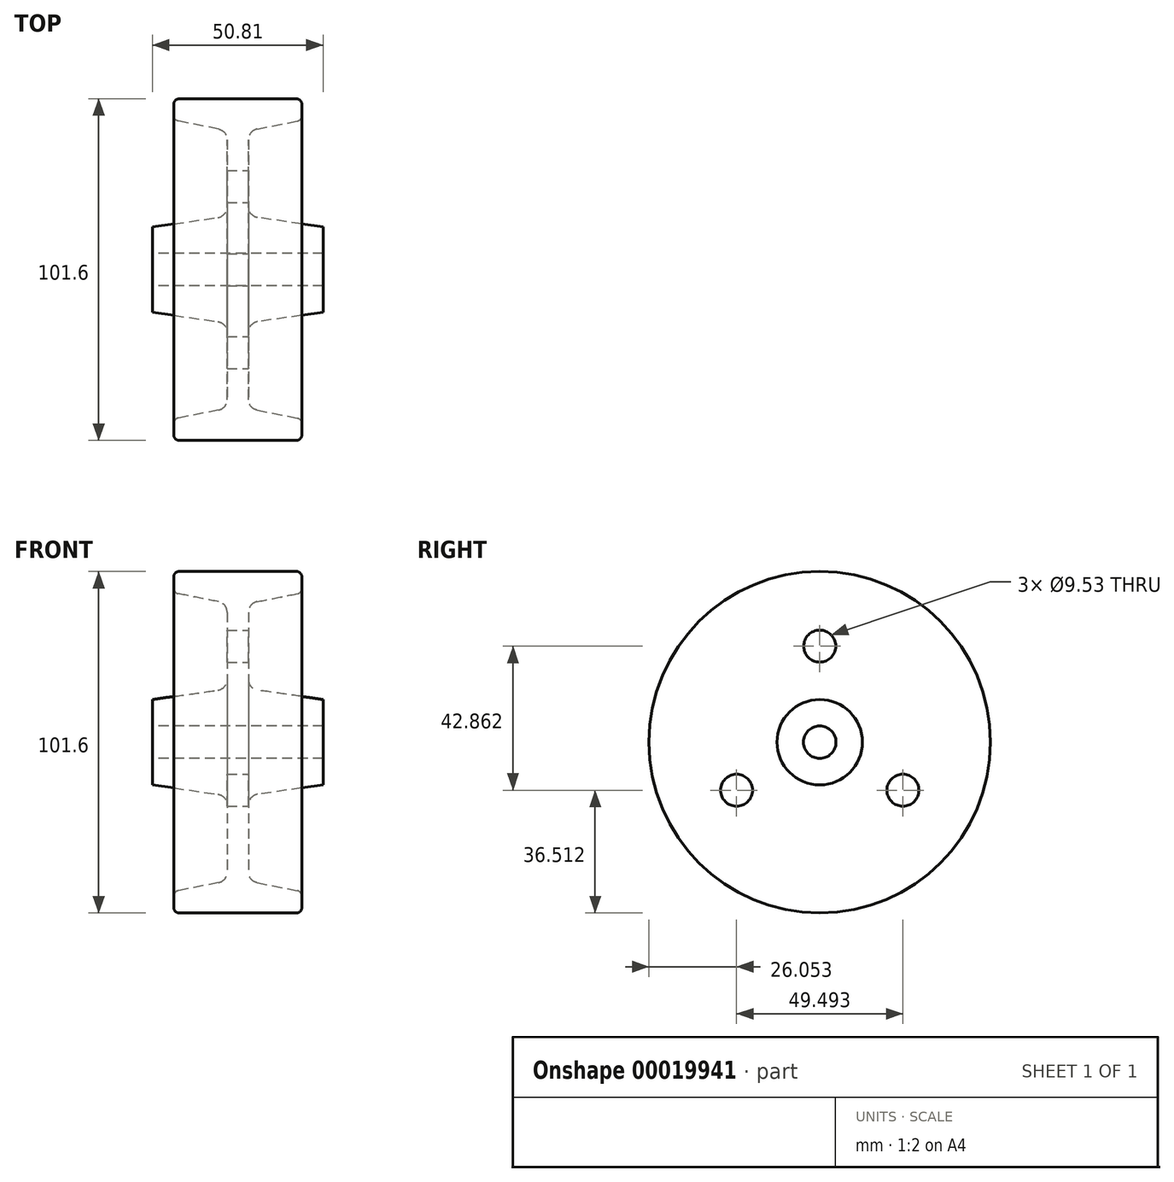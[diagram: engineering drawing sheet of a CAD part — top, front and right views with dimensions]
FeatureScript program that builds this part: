
annotation { "Feature Type Name" : "Feature", "Feature Type Description" : "" }
export const myFeature = defineFeature(function(context is Context, id is Id, definition is map)
    precondition{}
    {
        {
            var Q0;
            Q0=qCreatedBy(makeId("Front.planeOp"),FACE);
            var sketch = newSketch(context, id + "F0", { "sketchPlane" : qUnion([Q0])});
            skLineSegment(sketch, "E0", {"start": v(-28.58, 202.5) * mm, "end": v(22.23, 202.5) * mm});
            skLineSegment(sketch, "E1", {"start": v(-6.35, 168.66) * mm, "end": v(-6.35, 188.7) * mm});
            skLineSegment(sketch, "E2", {"start": v(-22.23, 162.88) * mm, "end": v(-22.23, 156.53) * mm});
            skLineSegment(sketch, "E3", {"start": v(-22.23, 156.53) * mm, "end": v(15.88, 156.53) * mm});
            skLineSegment(sketch, "E4", {"start": v(15.88, 156.53) * mm, "end": v(15.88, 162.88) * mm});
            skLineSegment(sketch, "E5", {"start": v(-28.58, 202.5) * mm, "end": v(-28.58, 194.63) * mm});
            skLineSegment(sketch, "E6", {"start": v(22.23, 202.5) * mm, "end": v(22.23, 194.63) * mm});
            skLineSegment(sketch, "E7", {"start": v(-22.23, 162.88) * mm, "end": v(-8.9, 165.54) * mm});
            skPoint(sketch, "E8.visualSharp", {"position": v(-6.35, 166.05) * mm});
            skArc(sketch, "E8.filletArc", {"start": v(-8.9, 165.54) * mm, "mid": v(-7.07, 166.64) * mm, "end": v(-6.35, 168.66) * mm});
            skPoint(sketch, "E9.visualSharp", {"position": v(-6.35, 191.45) * mm});
            skArc(sketch, "E9.filletArc", {"start": v(-6.35, 188.7) * mm, "mid": v(-7.13, 190.78) * mm, "end": v(-9.08, 191.84) * mm});
            skLineSegment(sketch, "E10", {"start": v(-28.58, 207.33) * mm, "end": v(22.22, 207.33) * mm});
            skLineSegment(sketch, "E11", {"start": v(15.88, 162.88) * mm, "end": v(2.55, 165.54) * mm});
            skPoint(sketch, "E12.visualSharp", {"position": v(0, 166.05) * mm});
            skArc(sketch, "E12.filletArc", {"start": v(0, 168.66) * mm, "mid": v(0.72, 166.64) * mm, "end": v(2.55, 165.54) * mm});
            skLineSegment(sketch, "E13", {"start": v(-28.58, 194.63) * mm, "end": v(-9.08, 191.84) * mm});
            skLineSegment(sketch, "E14", {"start": v(0, 168.66) * mm, "end": v(0, 188.7) * mm});
            skLineSegment(sketch, "E15", {"start": v(2.73, 191.84) * mm, "end": v(22.23, 194.63) * mm});
            skPoint(sketch, "E16.visualSharp", {"position": v(0, 191.45) * mm});
            skArc(sketch, "E16.filletArc", {"start": v(2.73, 191.84) * mm, "mid": v(0.78, 190.78) * mm, "end": v(0, 188.7) * mm});
            skSolve(sketch);
        }
        {
            var Q0;
            Q0=makeQuery(id+"F0.imprint","IMPRINT",FACE,{"disambiguationData":[TD([[makeQuery(id+"F0.imprint","IMPRINT",EDGE,{"derivedFrom":sQuery(id+"F0.wireOp",EDGE,"E0")}),-1.0]])]});
            var Q1;
            Q1=sQuery(id+"F0.wireOp",EDGE,"E10");
            revolve(context, id + "F1", {"entities" : qUnion([Q0]), "axis" : qUnion([Q1]), "revolveType" : RevolveType.FULL});
        }
        {
            var Q0;
            Q0=makeQuery(id+"F1.opRevolve","SWEPT_FACE",FACE,{"disambiguationData":[OSD([sQuery(id+"F0.wireOp",EDGE,"E14")])]});
            var sketch = newSketch(context, id + "F2", { "sketchPlane" : qUnion([Q0])});
            skCircle(sketch, "E17", {"center": v(-24.75, 193.04) * mm, "radius": 4.76 * mm});
            skCircle(sketch, "E18", {"center": v(0, 235.9) * mm, "radius": 4.76 * mm});
            skCircle(sketch, "E19", {"center": v(24.75, 193.04) * mm, "radius": 4.76 * mm});
            skSolve(sketch);
        }
        {
            var Q0;
            Q0=sQuery(id+"F2.wireOp",VERTEX,"E18.center");
            var Q1;
            Q1=sQuery(id+"F2.wireOp",VERTEX,"E17.center");
            var Q2;
            Q2=sQuery(id+"F2.wireOp",VERTEX,"E19.center");
            var Q3;
            Q3=makeQuery(id+"F1.opRevolve","SWEPT_BODY",BODY,{"disambiguationData":[OSD([sQuery(id+"F0.wireOp",EDGE,"E0"),sQuery(id+"F0.wireOp",EDGE,"E1"),sQuery(id+"F0.wireOp",EDGE,"E2"),sQuery(id+"F0.wireOp",EDGE,"E3"),sQuery(id+"F0.wireOp",EDGE,"E4"),sQuery(id+"F0.wireOp",EDGE,"E5"),sQuery(id+"F0.wireOp",EDGE,"E6"),sQuery(id+"F0.wireOp",EDGE,"E7"),sQuery(id+"F0.wireOp",EDGE,"E8.filletArc"),sQuery(id+"F0.wireOp",EDGE,"E9.filletArc"),sQuery(id+"F0.wireOp",EDGE,"E11"),sQuery(id+"F0.wireOp",EDGE,"E12.filletArc"),sQuery(id+"F0.wireOp",EDGE,"E13"),sQuery(id+"F0.wireOp",EDGE,"E14"),sQuery(id+"F0.wireOp",EDGE,"E15"),sQuery(id+"F0.wireOp",EDGE,"E16.filletArc")])]});
            hole(context, id + "F3", {"style" : HoleStyle.SIMPLE, "holeDiameter" : 9.52 * mm, "endStyle" : HoleEndStyle.THROUGH, "locations" : qUnion([Q0, Q1, Q2]), "scope" : qUnion([Q3])});
        }
        {
            var Q0;
            Q0=makeQuery(id+"F3.hole-1.boolean.opBoolean","INTERSECT",EDGE,{"derivedFrom":[makeQuery(id+"F1.opRevolve","SWEPT_FACE",FACE,{"disambiguationData":[OSD([sQuery(id+"F0.wireOp",EDGE,"E1")])]}),makeQuery(id+"F3.hole-1.opRevolve","SWEPT_FACE",FACE,{"disambiguationData":[OSD([sQuery(id+"F3.hole-1.sketch.wireOp",EDGE,"core_line_2")])]})]});
            var Q1;
            Q1=makeQuery(id+"F3.hole-2.boolean.opBoolean","INTERSECT",EDGE,{"derivedFrom":[makeQuery(id+"F1.opRevolve","SWEPT_FACE",FACE,{"disambiguationData":[OSD([sQuery(id+"F0.wireOp",EDGE,"E1")])]}),makeQuery(id+"F3.hole-2.opRevolve","SWEPT_FACE",FACE,{"disambiguationData":[OSD([sQuery(id+"F3.hole-2.sketch.wireOp",EDGE,"core_line_2")])]})]});
            var Q2;
            Q2=makeQuery(id+"F3.hole-0.boolean.opBoolean","INTERSECT",EDGE,{"derivedFrom":[makeQuery(id+"F1.opRevolve","SWEPT_FACE",FACE,{"disambiguationData":[OSD([sQuery(id+"F0.wireOp",EDGE,"E1")])]}),makeQuery(id+"F3.hole-0.opRevolve","SWEPT_FACE",FACE,{"disambiguationData":[OSD([sQuery(id+"F3.hole-0.sketch.wireOp",EDGE,"core_line_2")])]})]});
            var Q3;
            Q3=makeQuery(id+"F3.hole-1.boolean.opBoolean","COPY",EDGE,{"derivedFrom":makeQuery(id+"F3.hole-1.opRevolve","SWEPT_EDGE",EDGE,{"disambiguationData":[OSD([sQuery(id+"F3.hole-1.sketch.wireOp",EDGE,"core_line_2"),sQuery(id+"F3.hole-1.sketch.wireOp",EDGE,"core_line_3")])]})});
            var Q4;
            Q4=makeQuery(id+"F3.hole-2.boolean.opBoolean","COPY",EDGE,{"derivedFrom":makeQuery(id+"F3.hole-2.opRevolve","SWEPT_EDGE",EDGE,{"disambiguationData":[OSD([sQuery(id+"F3.hole-2.sketch.wireOp",EDGE,"core_line_2"),sQuery(id+"F3.hole-2.sketch.wireOp",EDGE,"core_line_3")])]})});
            var Q5;
            Q5=makeQuery(id+"F3.hole-0.boolean.opBoolean","COPY",EDGE,{"derivedFrom":makeQuery(id+"F3.hole-0.opRevolve","SWEPT_EDGE",EDGE,{"disambiguationData":[OSD([sQuery(id+"F3.hole-0.sketch.wireOp",EDGE,"core_line_2"),sQuery(id+"F3.hole-0.sketch.wireOp",EDGE,"core_line_3")])]})});
            var Q6;
            Q6=makeQuery(id+"F1.opRevolve","SWEPT_EDGE",EDGE,{"disambiguationData":[OSD([sQuery(id+"F0.wireOp",EDGE,"E2"),sQuery(id+"F0.wireOp",EDGE,"E7")])]});
            var Q7;
            Q7=makeQuery(id+"F1.opRevolve","SWEPT_EDGE",EDGE,{"disambiguationData":[OSD([sQuery(id+"F0.wireOp",EDGE,"E2"),sQuery(id+"F0.wireOp",EDGE,"E3")])]});
            var Q8;
            Q8=makeQuery(id+"F1.opRevolve","SWEPT_EDGE",EDGE,{"disambiguationData":[OSD([sQuery(id+"F0.wireOp",EDGE,"E3"),sQuery(id+"F0.wireOp",EDGE,"E4")])]});
            var Q9;
            Q9=makeQuery(id+"F1.opRevolve","SWEPT_EDGE",EDGE,{"disambiguationData":[OSD([sQuery(id+"F0.wireOp",EDGE,"E4"),sQuery(id+"F0.wireOp",EDGE,"E11")])]});
            fillet(context, id + "F4", {"entities" : qUnion([Q0, Q1, Q2, Q3, Q4, Q5, Q6, Q7, Q8, Q9]), "radius" : 1.59 * mm, "tangentPropagation" : true, "allowEdgeOverflow" : false});
        }
    });
